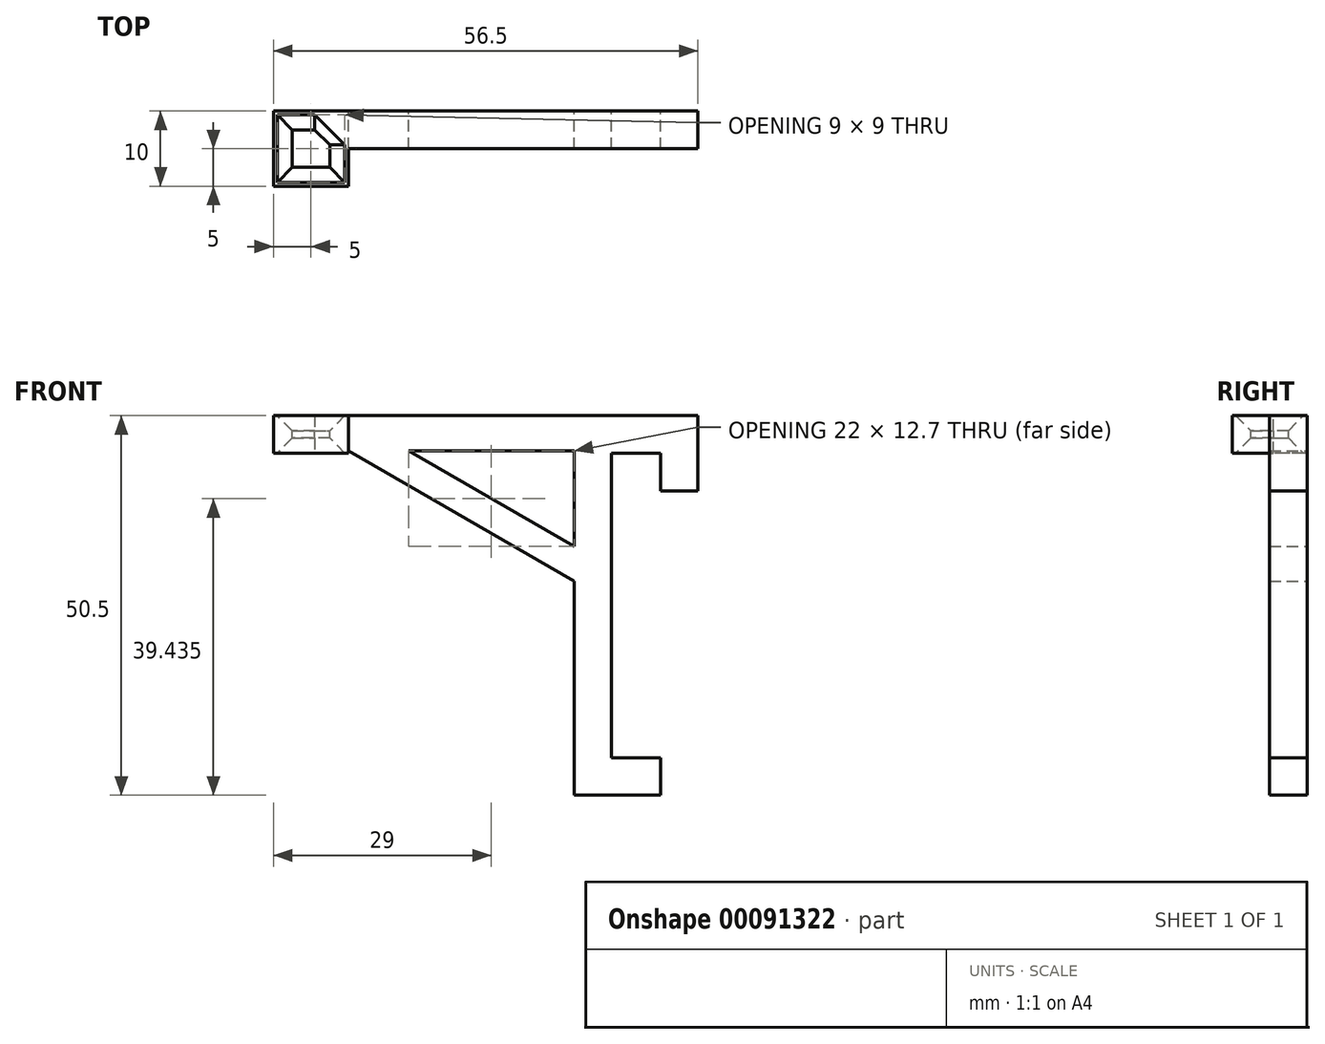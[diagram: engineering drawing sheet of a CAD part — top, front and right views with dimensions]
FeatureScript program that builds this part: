
annotation { "Feature Type Name" : "Feature", "Feature Type Description" : "" }
export const myFeature = defineFeature(function(context is Context, id is Id, definition is map)
    precondition{}
    {
        {
            var Q0;
            Q0=qCreatedBy(makeId("Front.planeOp"),FACE);
            var sketch = newSketch(context, id + "F0", { "sketchPlane" : qUnion([Q0])});
            skLineSegment(sketch, "E0.bottom", {"start": v(0, 50.5) * mm, "end": v(5, 50.5) * mm});
            skLineSegment(sketch, "E0.top", {"start": v(0, 0) * mm, "end": v(5, 0) * mm});
            skLineSegment(sketch, "E0.left", {"start": v(0, 50.5) * mm, "end": v(0, 0) * mm});
            skLineSegment(sketch, "E0.right", {"start": v(5, 50.5) * mm, "end": v(5, 0) * mm});
            skLineSegment(sketch, "E1.bottom", {"start": v(5, 0) * mm, "end": v(11.5, 0) * mm});
            skLineSegment(sketch, "E1.top", {"start": v(5, 5) * mm, "end": v(11.5, 5) * mm});
            skLineSegment(sketch, "E1.left", {"start": v(5, 0) * mm, "end": v(5, 5) * mm});
            skLineSegment(sketch, "E1.right", {"start": v(11.5, 0) * mm, "end": v(11.5, 5) * mm});
            skLineSegment(sketch, "E2.bottom", {"start": v(5, 50.5) * mm, "end": v(16.5, 50.5) * mm});
            skLineSegment(sketch, "E2.top", {"start": v(5, 45.5) * mm, "end": v(16.5, 45.5) * mm});
            skLineSegment(sketch, "E2.left", {"start": v(5, 50.5) * mm, "end": v(5, 45.5) * mm});
            skLineSegment(sketch, "E2.right", {"start": v(16.5, 50.5) * mm, "end": v(16.5, 45.5) * mm});
            skLineSegment(sketch, "E3.bottom", {"start": v(16.5, 45.5) * mm, "end": v(11.5, 45.5) * mm});
            skLineSegment(sketch, "E3.top", {"start": v(16.5, 40.5) * mm, "end": v(11.5, 40.5) * mm});
            skLineSegment(sketch, "E3.left", {"start": v(16.5, 45.5) * mm, "end": v(16.5, 40.5) * mm});
            skLineSegment(sketch, "E3.right", {"start": v(11.5, 45.5) * mm, "end": v(11.5, 40.5) * mm});
            skLineSegment(sketch, "E4.bottom", {"start": v(0, 50.5) * mm, "end": v(-30, 50.5) * mm});
            skLineSegment(sketch, "E4.top", {"start": v(0, 45.79) * mm, "end": v(-30, 45.79) * mm});
            skLineSegment(sketch, "E4.left", {"start": v(0, 50.5) * mm, "end": v(0, 45.79) * mm});
            skLineSegment(sketch, "E4.right", {"start": v(-30, 50.5) * mm, "end": v(-30, 45.79) * mm});
            skLineSegment(sketch, "E5", {"start": v(-30, 45.79) * mm, "end": v(0, 28.47) * mm});
            skLineSegment(sketch, "E6", {"start": v(-22, 45.79) * mm, "end": v(0, 33.08) * mm});
            skSolve(sketch);
        }
        {
            var Q0;
            Q0 = qSketchRegion(id + "F0", true);
            extrude(context, id + "F1", {"entities" : qUnion([Q0]), "depth" : 5 * mm});
        }
        {
            var Q0;
            Q0=makeQuery(id+"F1.opExtrude","SWEPT_FACE",FACE,{"disambiguationData":[OSD([sQuery(id+"F0.wireOp",EDGE,"E0.bottom"),sQuery(id+"F0.wireOp",EDGE,"E2.bottom"),sQuery(id+"F0.wireOp",EDGE,"E4.bottom")])]});
            var sketch = newSketch(context, id + "F2", { "sketchPlane" : qUnion([Q0])});
            skLineSegment(sketch, "E7.0", {"start": v(-30, -5) * mm, "end": v(-30, 0) * mm, "construction": true});
            skLineSegment(sketch, "E8.bottom", {"start": v(-30, 0) * mm, "end": v(-40, 0) * mm});
            skLineSegment(sketch, "E8.top", {"start": v(-30, -10) * mm, "end": v(-40, -10) * mm});
            skLineSegment(sketch, "E8.left", {"start": v(-30, 0) * mm, "end": v(-30, -10) * mm});
            skLineSegment(sketch, "E8.right", {"start": v(-40, 0) * mm, "end": v(-40, -10) * mm});
            skLineSegment(sketch, "E9.0", {"start": v(-37.5, -2.5) * mm, "end": v(-37.5, -7.5) * mm});
            skLineSegment(sketch, "E9.1", {"start": v(-32.5, -2.5) * mm, "end": v(-37.5, -2.5) * mm});
            skLineSegment(sketch, "E9.2", {"start": v(-32.5, -2.5) * mm, "end": v(-32.5, -7.5) * mm});
            skLineSegment(sketch, "E9.3", {"start": v(-32.5, -7.5) * mm, "end": v(-37.5, -7.5) * mm});
            skSolve(sketch);
        }
        {
            var Q0;
            {var subQ1=sQuery(id+"F2.wireOp",EDGE,"E8.bottom");Q0=makeQuery(id+"F2.imprint","IMPRINT",FACE,{"disambiguationData":[TD([[makeQuery(id+"F2.imprint","IMPRINT",EDGE,{"derivedFrom":subQ1}),1.0]])]});}
            var Q1;
            Q1=makeQuery(id+"F1.opExtrude","SWEPT_BODY",BODY,{"disambiguationData":[OSD([sQuery(id+"F0.wireOp",EDGE,"E0.bottom"),sQuery(id+"F0.wireOp",EDGE,"E0.top"),sQuery(id+"F0.wireOp",EDGE,"E0.left"),sQuery(id+"F0.wireOp",EDGE,"E0.right"),sQuery(id+"F0.wireOp",EDGE,"E1.bottom"),sQuery(id+"F0.wireOp",EDGE,"E1.top"),sQuery(id+"F0.wireOp",EDGE,"E1.right"),sQuery(id+"F0.wireOp",EDGE,"E2.bottom"),sQuery(id+"F0.wireOp",EDGE,"E2.top"),sQuery(id+"F0.wireOp",EDGE,"E2.right"),sQuery(id+"F0.wireOp",EDGE,"E3.top"),sQuery(id+"F0.wireOp",EDGE,"E3.left"),sQuery(id+"F0.wireOp",EDGE,"E3.right"),sQuery(id+"F0.wireOp",EDGE,"E4.bottom"),sQuery(id+"F0.wireOp",EDGE,"E4.top"),sQuery(id+"F0.wireOp",EDGE,"E4.right"),sQuery(id+"F0.wireOp",EDGE,"E5"),sQuery(id+"F0.wireOp",EDGE,"E6")])]});
            extrude(context, id + "F3", {"entities" : qUnion([Q0]), "operationType" : NewBodyOperationType.ADD, "oppositeDirection" : true, "endBoundEntityBody" : qUnion([Q1]), "depth" : 5 * mm});
        }
        {
            var Q0;
            Q0=makeQuery(id+"F3.opExtrude","CAP_EDGE",EDGE,{"disambiguationData":[OSD([sQuery(id+"F2.wireOp",EDGE,"E9.2")])],"isStart":true});
            var Q1;
            Q1=makeQuery(id+"F3.opExtrude","CAP_EDGE",EDGE,{"disambiguationData":[OSD([sQuery(id+"F2.wireOp",EDGE,"E9.1")])],"isStart":true});
            var Q2;
            Q2=makeQuery(id+"F3.opExtrude","CAP_EDGE",EDGE,{"disambiguationData":[OSD([sQuery(id+"F2.wireOp",EDGE,"E9.0")])],"isStart":true});
            var Q3;
            Q3=makeQuery(id+"F3.opExtrude","CAP_EDGE",EDGE,{"disambiguationData":[OSD([sQuery(id+"F2.wireOp",EDGE,"E9.3")])],"isStart":true});
            var Q4;
            Q4=makeQuery(id+"F3.opExtrude","SWEPT_EDGE",EDGE,{"disambiguationData":[OSD([sQuery(id+"F2.wireOp",EDGE,"E9.1"),sQuery(id+"F2.wireOp",EDGE,"E9.2")])]});
            var Q5;
            Q5=makeQuery(id+"F3.opExtrude","CAP_EDGE",EDGE,{"disambiguationData":[OSD([sQuery(id+"F2.wireOp",EDGE,"E9.2")])],"isStart":false});
            var Q6;
            Q6=makeQuery(id+"F3.opExtrude","CAP_EDGE",EDGE,{"disambiguationData":[OSD([sQuery(id+"F2.wireOp",EDGE,"E9.3")])],"isStart":false});
            var Q7;
            Q7=makeQuery(id+"F3.opExtrude","CAP_EDGE",EDGE,{"disambiguationData":[OSD([sQuery(id+"F2.wireOp",EDGE,"E9.0")])],"isStart":false});
            chamfer(context, id + "F4", {"entities" : qUnion([Q0, Q1, Q2, Q3, Q4, Q5, Q6, Q7]), "width" : 2 * mm, "tangentPropagation" : true});
        }
    });
